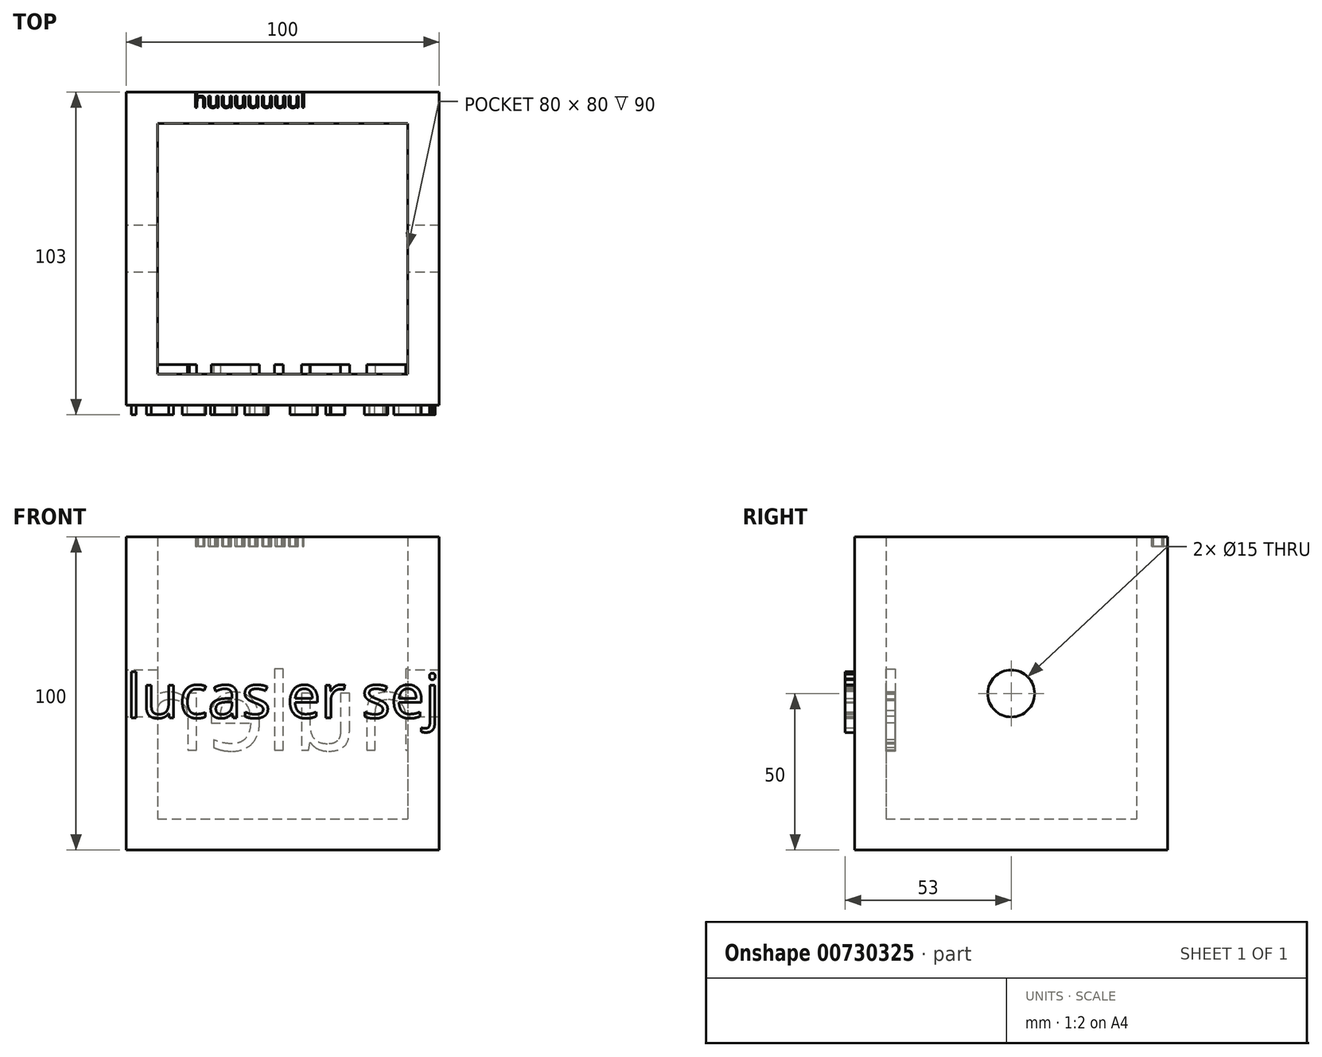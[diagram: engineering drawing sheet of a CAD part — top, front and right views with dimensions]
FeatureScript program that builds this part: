
annotation { "Feature Type Name" : "Feature", "Feature Type Description" : "" }
export const myFeature = defineFeature(function(context is Context, id is Id, definition is map)
    precondition{}
    {
        {
            var Q0;
            Q0=qCreatedBy(makeId("Top.planeOp"),FACE);
            var sketch = newSketch(context, id + "F0", { "sketchPlane" : qUnion([Q0])});
            skLineSegment(sketch, "E0.bottom", {"start": v(0, 0) * mm, "end": v(100, 0) * mm});
            skLineSegment(sketch, "E0.top", {"start": v(0, 100) * mm, "end": v(100, 100) * mm});
            skLineSegment(sketch, "E0.left", {"start": v(0, 0) * mm, "end": v(0, 100) * mm});
            skLineSegment(sketch, "E0.right", {"start": v(100, 0) * mm, "end": v(100, 100) * mm});
            skSolve(sketch);
        }
        {
            var Q0;
            Q0 = qSketchRegion(id + "F0", true);
            extrude(context, id + "F1", {"entities" : qUnion([Q0]), "depth" : 100 * mm, "offsetDistance" : 25.4 * mm});
        }
        {
            var Q0;
            Q0=makeQuery(id+"F1.opExtrude","CAP_FACE",FACE,{"disambiguationData":[OSD([sQuery(id+"F0.wireOp",EDGE,"E0.bottom"),sQuery(id+"F0.wireOp",EDGE,"E0.top"),sQuery(id+"F0.wireOp",EDGE,"E0.left"),sQuery(id+"F0.wireOp",EDGE,"E0.right")])],"isStart":false});
            shell(context, id + "F2", {"entities" : qUnion([Q0]), "thickness" : 10 * mm});
        }
        {
            var Q0;
            Q0=makeQuery(id+"F1.opExtrude","SWEPT_FACE",FACE,{"disambiguationData":[OSD([sQuery(id+"F0.wireOp",EDGE,"E0.left")])]});
            var sketch = newSketch(context, id + "F3", { "sketchPlane" : qUnion([Q0])});
            skCircle(sketch, "E1", {"center": v(-50, 50) * mm, "radius": 7.5 * mm});
            skSolve(sketch);
        }
        {
            var Q0;
            Q0 = qSketchRegion(id + "F3", true);
            extrude(context, id + "F4", {"entities" : qUnion([Q0]), "operationType" : NewBodyOperationType.REMOVE, "oppositeDirection" : true, "depth" : 100 * mm, "offsetDistance" : 25.4 * mm});
        }
        {
            var Q0;
            Q0=makeQuery(id+"F1.opExtrude","SWEPT_FACE",FACE,{"disambiguationData":[OSD([sQuery(id+"F0.wireOp",EDGE,"E0.bottom")])]});
            var sketch = newSketch(context, id + "F5", { "sketchPlane" : qUnion([Q0])});
            skText(sketch, "E2", { "text": "lucas er sej", "fontName": "OpenSans-Regular.ttf"});
            const initialGuessF5  = {"E2": [0, 0.04222, 1, 0, 0.014]};
            skSetInitialGuess(sketch, initialGuessF5);
            skSolve(sketch);
        }
        {
            var Q0;
            Q0 = qSketchRegion(id + "F5", true);
            extrude(context, id + "F6", {"entities" : qUnion([Q0]), "operationType" : NewBodyOperationType.ADD, "depth" : 3 * mm, "offsetDistance" : 25.4 * mm});
        }
        {
            var Q0;
            Q0=makeQuery(id+"F2.opShell","OFFSET_FACE",FACE,{"disambiguationData":[OSD([sQuery(id+"F0.wireOp",EDGE,"E0.bottom")])]});
            var sketch = newSketch(context, id + "F7", { "sketchPlane" : qUnion([Q0])});
            skText(sketch, "E3", { "text": "hulen", "fontName": "OpenSans-Regular.ttf"});
            const initialGuessF7  = {"E3": [-0.095, 0.0319, 1, 0, 0.02455]};
            skSetInitialGuess(sketch, initialGuessF7);
            skSolve(sketch);
        }
        {
            var Q0;
            Q0 = qSketchRegion(id + "F7", true);
            extrude(context, id + "F8", {"entities" : qUnion([Q0]), "operationType" : NewBodyOperationType.ADD, "depth" : 3 * mm, "offsetDistance" : 25.4 * mm});
        }
        {
            var Q0;
            Q0=makeQuery(id+"F1.opExtrude","CAP_FACE",FACE,{"disambiguationData":[OSD([sQuery(id+"F0.wireOp",EDGE,"E0.bottom"),sQuery(id+"F0.wireOp",EDGE,"E0.top"),sQuery(id+"F0.wireOp",EDGE,"E0.left"),sQuery(id+"F0.wireOp",EDGE,"E0.right")])],"isStart":false});
            var sketch = newSketch(context, id + "F9", { "sketchPlane" : qUnion([Q0])});
            skText(sketch, "E4", { "text": "huuuuuuul", "fontName": "OpenSans-Regular.ttf"});
            const initialGuessF9  = {"E4": [0.02153, 0.095, 1, 0, 0.005]};
            skSetInitialGuess(sketch, initialGuessF9);
            skSolve(sketch);
        }
        {
            var Q0;
            Q0 = qSketchRegion(id + "F9", true);
            extrude(context, id + "F10", {"entities" : qUnion([Q0]), "operationType" : NewBodyOperationType.REMOVE, "oppositeDirection" : true, "depth" : 3 * mm, "offsetDistance" : 25.4 * mm});
        }
    });
